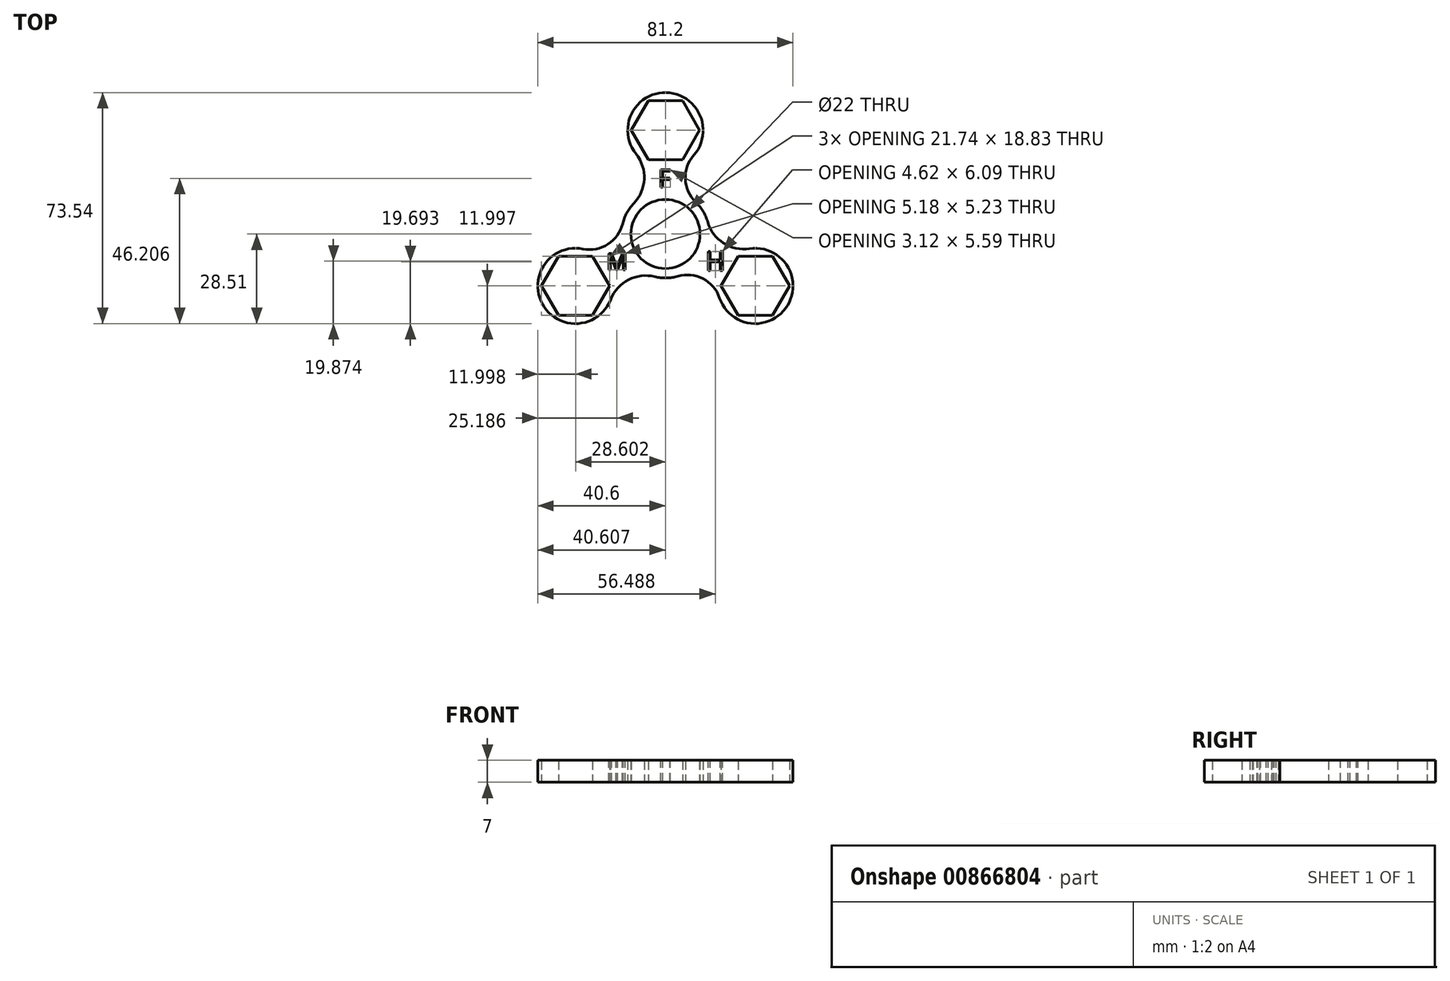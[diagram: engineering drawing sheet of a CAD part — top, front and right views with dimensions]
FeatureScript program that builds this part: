
annotation { "Feature Type Name" : "Feature", "Feature Type Description" : "" }
export const myFeature = defineFeature(function(context is Context, id is Id, definition is map)
    precondition{}
    {
        {
            var Q0;
            Q0=qCreatedBy(makeId("Top.planeOp"),FACE);
            var sketch = newSketch(context, id + "F0", { "sketchPlane" : qUnion([Q0])});
            skCircle(sketch, "E0", {"center": v(0, 0) * mm, "radius": 11 * mm});
            skCircle(sketch, "E1", {"center": v(0, 0) * mm, "radius": 45.03 * mm, "construction": true});
            skCircle(sketch, "E2", {"center": v(0, 0) * mm, "radius": 14 * mm});
            skCircle(sketch, "E3", {"center": v(0, 33.03) * mm, "radius": 12 * mm});
            skArc(sketch, "E4", {"start": v(-10.07, 9.73) * mm, "mid": v(-6.73, 17.48) * mm, "end": v(-9.35, 25.5) * mm});
            skArc(sketch, "E5", {"start": v(9.03, 25.12) * mm, "mid": v(6.35, 17.48) * mm, "end": v(9.69, 10.1) * mm});
            skCircle(sketch, "E6.1.1", {"center": v(-28.6, -16.51) * mm, "radius": 12 * mm});
            skArc(sketch, "E6.1.2", {"start": v(-3.39, -13.58) * mm, "mid": v(-11.78, -14.57) * mm, "end": v(-17.41, -20.85) * mm});
            skArc(sketch, "E6.1.3", {"start": v(-26.27, -4.74) * mm, "mid": v(-18.31, -3.24) * mm, "end": v(-13.6, 3.34) * mm});
            skCircle(sketch, "E6.2.1", {"center": v(28.6, -16.51) * mm, "radius": 12 * mm});
            skArc(sketch, "E6.2.2", {"start": v(13.46, 3.86) * mm, "mid": v(18.5, -2.91) * mm, "end": v(26.76, -4.65) * mm});
            skArc(sketch, "E6.2.3", {"start": v(17.24, -20.38) * mm, "mid": v(11.97, -14.24) * mm, "end": v(3.9, -13.44) * mm});
            skCircle(sketch, "E7.cCircle", {"center": v(0, 33.03) * mm, "radius": 9.42 * mm, "construction": true});
            skLineSegment(sketch, "E7.0", {"start": v(5.44, 23.61) * mm, "end": v(-5.44, 23.61) * mm});
            skLineSegment(sketch, "E7.1", {"start": v(-5.44, 23.61) * mm, "end": v(-10.87, 33.03) * mm});
            skLineSegment(sketch, "E7.2", {"start": v(-10.87, 33.03) * mm, "end": v(-5.44, 42.44) * mm});
            skLineSegment(sketch, "E7.3", {"start": v(-5.44, 42.44) * mm, "end": v(5.44, 42.44) * mm});
            skLineSegment(sketch, "E7.4", {"start": v(5.44, 42.44) * mm, "end": v(10.87, 33.03) * mm});
            skLineSegment(sketch, "E7.5", {"start": v(10.87, 33.03) * mm, "end": v(5.44, 23.61) * mm});
            skPoint(sketch, "E7.0.midPoint", {"position": v(0, 23.61) * mm});
            skCircle(sketch, "E8.1.0", {"center": v(-28.6, -16.51) * mm, "radius": 9.42 * mm, "construction": true});
            skLineSegment(sketch, "E8.1.1", {"start": v(-34.04, -25.93) * mm, "end": v(-39.47, -16.51) * mm});
            skLineSegment(sketch, "E8.1.2", {"start": v(-39.47, -16.51) * mm, "end": v(-34.04, -7.1) * mm});
            skLineSegment(sketch, "E8.1.3", {"start": v(-34.04, -7.1) * mm, "end": v(-23.17, -7.1) * mm});
            skLineSegment(sketch, "E8.1.4", {"start": v(-23.17, -7.1) * mm, "end": v(-17.73, -16.51) * mm});
            skLineSegment(sketch, "E8.1.5", {"start": v(-17.73, -16.51) * mm, "end": v(-23.17, -25.93) * mm});
            skLineSegment(sketch, "E8.1.6", {"start": v(-23.17, -25.93) * mm, "end": v(-34.04, -25.93) * mm});
            skCircle(sketch, "E8.2.0", {"center": v(28.6, -16.51) * mm, "radius": 9.42 * mm, "construction": true});
            skLineSegment(sketch, "E8.2.1", {"start": v(39.47, -16.51) * mm, "end": v(34.04, -25.93) * mm});
            skLineSegment(sketch, "E8.2.2", {"start": v(34.04, -25.93) * mm, "end": v(23.17, -25.93) * mm});
            skLineSegment(sketch, "E8.2.3", {"start": v(23.17, -25.93) * mm, "end": v(17.73, -16.51) * mm});
            skLineSegment(sketch, "E8.2.4", {"start": v(17.73, -16.51) * mm, "end": v(23.17, -7.1) * mm});
            skLineSegment(sketch, "E8.2.5", {"start": v(23.17, -7.1) * mm, "end": v(34.04, -7.1) * mm});
            skLineSegment(sketch, "E8.2.6", {"start": v(34.04, -7.1) * mm, "end": v(39.47, -16.51) * mm});
            skSolve(sketch);
        }
        {
            var Q0;
            {var subQ0=sQuery(id+"F0.wireOp",EDGE,"E4");Q0=makeQuery(id+"F0.imprint","IMPRINT",FACE,{"disambiguationData":[TD([[makeQuery(id+"F0.imprint","IMPRINT",EDGE,{"derivedFrom":subQ0}),-1.0]])]});}
            var Q1;
            Q1=makeQuery(id+"F0.imprint","IMPRINT",FACE,{"disambiguationData":[TD([[makeQuery(id+"F0.imprint","IMPRINT",EDGE,{"derivedFrom":sQuery(id+"F0.wireOp",EDGE,"E0")}),-1.0]])]});
            var Q2;
            {var subQ0=sQuery(id+"F0.wireOp",EDGE,"E6.1.2");Q2=makeQuery(id+"F0.imprint","IMPRINT",FACE,{"disambiguationData":[TD([[makeQuery(id+"F0.imprint","IMPRINT",EDGE,{"derivedFrom":subQ0}),-1.0]])]});}
            var Q3;
            {var subQ0=sQuery(id+"F0.wireOp",EDGE,"E6.2.2");Q3=makeQuery(id+"F0.imprint","IMPRINT",FACE,{"disambiguationData":[TD([[makeQuery(id+"F0.imprint","IMPRINT",EDGE,{"derivedFrom":subQ0}),-1.0]])]});}
            var Q4;
            Q4=makeQuery(id+"F0.imprint","IMPRINT",FACE,{"disambiguationData":[TD([[makeQuery(id+"F0.imprint","IMPRINT",EDGE,{"derivedFrom":sQuery(id+"F0.wireOp",EDGE,"E7.0")}),1.0]])]});
            var Q5;
            Q5=makeQuery(id+"F0.imprint","IMPRINT",FACE,{"disambiguationData":[TD([[makeQuery(id+"F0.imprint","IMPRINT",EDGE,{"derivedFrom":sQuery(id+"F0.wireOp",EDGE,"E8.1.1")}),1.0]])]});
            var Q6;
            Q6=makeQuery(id+"F0.imprint","IMPRINT",FACE,{"disambiguationData":[TD([[makeQuery(id+"F0.imprint","IMPRINT",EDGE,{"derivedFrom":sQuery(id+"F0.wireOp",EDGE,"E8.2.1")}),1.0]])]});
            extrude(context, id + "F1", {"entities" : qUnion([Q0, Q1, Q2, Q3, Q4, Q5, Q6]), "depth" : 7 * mm, "offsetDistance" : 25 * mm, "symmetric" : true});
        }
        {
            var Q0;
            Q0=makeQuery(id+"F1.opExtrude","CAP_FACE",FACE,{"disambiguationData":[OSD([sQuery(id+"F0.wireOp",EDGE,"E0"),sQuery(id+"F0.wireOp",EDGE,"E2"),sQuery(id+"F0.wireOp",EDGE,"E3"),sQuery(id+"F0.wireOp",EDGE,"E4"),sQuery(id+"F0.wireOp",EDGE,"E5"),sQuery(id+"F0.wireOp",EDGE,"E6.1.1"),sQuery(id+"F0.wireOp",EDGE,"E6.1.2"),sQuery(id+"F0.wireOp",EDGE,"E6.1.3"),sQuery(id+"F0.wireOp",EDGE,"E6.2.1"),sQuery(id+"F0.wireOp",EDGE,"E6.2.2"),sQuery(id+"F0.wireOp",EDGE,"E6.2.3"),sQuery(id+"F0.wireOp",EDGE,"E7.0"),sQuery(id+"F0.wireOp",EDGE,"E7.1"),sQuery(id+"F0.wireOp",EDGE,"E7.2"),sQuery(id+"F0.wireOp",EDGE,"E7.3"),sQuery(id+"F0.wireOp",EDGE,"E7.4"),sQuery(id+"F0.wireOp",EDGE,"E7.5"),sQuery(id+"F0.wireOp",EDGE,"E8.1.1"),sQuery(id+"F0.wireOp",EDGE,"E8.1.2"),sQuery(id+"F0.wireOp",EDGE,"E8.1.3"),sQuery(id+"F0.wireOp",EDGE,"E8.1.4"),sQuery(id+"F0.wireOp",EDGE,"E8.1.5"),sQuery(id+"F0.wireOp",EDGE,"E8.1.6"),sQuery(id+"F0.wireOp",EDGE,"E8.2.1"),sQuery(id+"F0.wireOp",EDGE,"E8.2.2"),sQuery(id+"F0.wireOp",EDGE,"E8.2.3"),sQuery(id+"F0.wireOp",EDGE,"E8.2.4"),sQuery(id+"F0.wireOp",EDGE,"E8.2.5"),sQuery(id+"F0.wireOp",EDGE,"E8.2.6")])],"isStart":false});
            var sketch = newSketch(context, id + "F2", { "sketchPlane" : qUnion([Q0])});
            skText(sketch, "E9", { "text": "F", "fontName": "OpenSans-Regular.ttf"});
            skText(sketch, "E10", { "text": "M", "fontName": "OpenSans-Regular.ttf"});
            skText(sketch, "E11", { "text": "H", "fontName": "OpenSans-Regular.ttf"});
            const initialGuessF2  = {"E9": [-0.00232, 0.0149, 1, 0, 0.00564], "E10": [-0.01872, -0.01143, 1, 0, 0.00527], "E11": [0.01274, -0.01168, 1, 0, 0.00614]};
            skSetInitialGuess(sketch, initialGuessF2);
            skSolve(sketch);
        }
        {
            var Q0;
            Q0=qSketchRegion(id+"F2",true);
            extrude(context, id + "F3", {"entities" : qUnion([Q0]), "operationType" : NewBodyOperationType.REMOVE, "oppositeDirection" : true, "depth" : 25 * mm, "offsetDistance" : 25 * mm});
        }
    });
